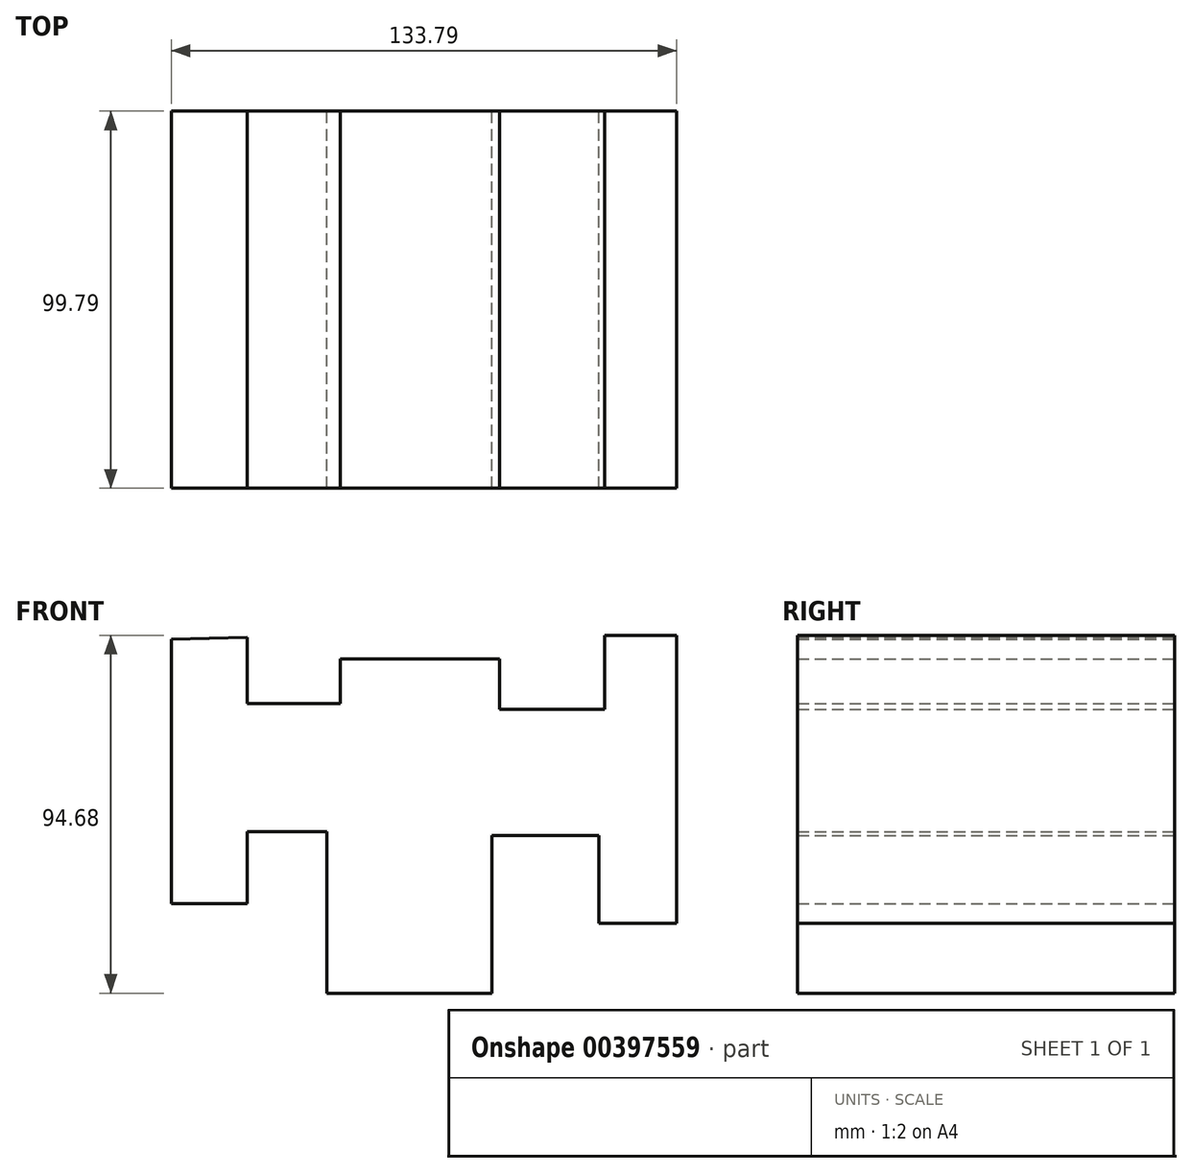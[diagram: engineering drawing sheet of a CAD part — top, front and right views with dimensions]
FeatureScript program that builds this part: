
annotation { "Feature Type Name" : "Feature", "Feature Type Description" : "" }
export const myFeature = defineFeature(function(context is Context, id is Id, definition is map)
    precondition{}
    {
        {
            var Q0;
            Q0=qCreatedBy(makeId("Front.planeOp"),FACE);
            var sketch = newSketch(context, id + "F0", { "sketchPlane" : qUnion([Q0])});
            skLineSegment(sketch, "E0", {"start": v(-62.78, 37.82) * mm, "end": v(-62.78, -32.16) * mm});
            skLineSegment(sketch, "E1", {"start": v(-62.78, -32.16) * mm, "end": v(-42.7, -32.16) * mm});
            skLineSegment(sketch, "E2", {"start": v(-42.7, -32.16) * mm, "end": v(-42.7, -13.12) * mm});
            skLineSegment(sketch, "E3", {"start": v(-42.7, -13.12) * mm, "end": v(-21.61, -13.12) * mm});
            skLineSegment(sketch, "E4", {"start": v(-21.61, -13.12) * mm, "end": v(-21.61, -55.83) * mm});
            skLineSegment(sketch, "E5", {"start": v(-21.61, -55.83) * mm, "end": v(22.13, -55.83) * mm});
            skLineSegment(sketch, "E6", {"start": v(22.13, -55.83) * mm, "end": v(22.13, -14.15) * mm});
            skLineSegment(sketch, "E7", {"start": v(22.13, -14.15) * mm, "end": v(50.43, -14.15) * mm});
            skLineSegment(sketch, "E8", {"start": v(50.43, -14.15) * mm, "end": v(50.43, -37.3) * mm});
            skLineSegment(sketch, "E9", {"start": v(50.43, -37.3) * mm, "end": v(71, -37.3) * mm});
            skLineSegment(sketch, "E10", {"start": v(71, -37.3) * mm, "end": v(71, 38.85) * mm});
            skLineSegment(sketch, "E11", {"start": v(71, 38.85) * mm, "end": v(51.97, 38.85) * mm});
            skLineSegment(sketch, "E12", {"start": v(51.97, 38.85) * mm, "end": v(51.97, 19.3) * mm});
            skLineSegment(sketch, "E13", {"start": v(51.97, 19.3) * mm, "end": v(24.18, 19.3) * mm});
            skLineSegment(sketch, "E14", {"start": v(24.18, 19.3) * mm, "end": v(24.18, 32.67) * mm});
            skLineSegment(sketch, "E15", {"start": v(24.18, 32.67) * mm, "end": v(-18, 32.67) * mm});
            skLineSegment(sketch, "E16", {"start": v(-18, 32.67) * mm, "end": v(-18, 20.84) * mm});
            skLineSegment(sketch, "E17", {"start": v(-18, 20.84) * mm, "end": v(-42.7, 20.84) * mm});
            skLineSegment(sketch, "E18", {"start": v(-42.7, 20.84) * mm, "end": v(-42.7, 38.33) * mm});
            skLineSegment(sketch, "E19", {"start": v(-42.7, 38.33) * mm, "end": v(-62.78, 37.82) * mm});
            skSolve(sketch);
        }
        {
            var Q0;
            Q0=makeQuery(id+"F0.imprint","IMPRINT",FACE,{"disambiguationData":[TD([[makeQuery(id+"F0.imprint","IMPRINT",EDGE,{"derivedFrom":sQuery(id+"F0.wireOp",EDGE,"E0")}),1.0]])]});
            extrude(context, id + "F1", {"entities" : qUnion([Q0]), "depth" : 39.62 * mm});
        }
        {
            var Q0;
            Q0=makeQuery(id+"F1.opExtrude","CAP_FACE",FACE,{"disambiguationData":[OSD([sQuery(id+"F0.wireOp",EDGE,"E0"),sQuery(id+"F0.wireOp",EDGE,"E1"),sQuery(id+"F0.wireOp",EDGE,"E2"),sQuery(id+"F0.wireOp",EDGE,"E3"),sQuery(id+"F0.wireOp",EDGE,"E4"),sQuery(id+"F0.wireOp",EDGE,"E5"),sQuery(id+"F0.wireOp",EDGE,"E6"),sQuery(id+"F0.wireOp",EDGE,"E7"),sQuery(id+"F0.wireOp",EDGE,"E8"),sQuery(id+"F0.wireOp",EDGE,"E9"),sQuery(id+"F0.wireOp",EDGE,"E10"),sQuery(id+"F0.wireOp",EDGE,"E11"),sQuery(id+"F0.wireOp",EDGE,"E12"),sQuery(id+"F0.wireOp",EDGE,"E13"),sQuery(id+"F0.wireOp",EDGE,"E14"),sQuery(id+"F0.wireOp",EDGE,"E15"),sQuery(id+"F0.wireOp",EDGE,"E16"),sQuery(id+"F0.wireOp",EDGE,"E17"),sQuery(id+"F0.wireOp",EDGE,"E18"),sQuery(id+"F0.wireOp",EDGE,"E19")])],"isStart":true});
            extrude(context, id + "F2", {"entities" : qUnion([Q0]), "operationType" : NewBodyOperationType.ADD, "depth" : 60.17 * mm});
        }
    });
